FCSTD DOCUMENT  (FreeCAD 0.19R24276 (Git))
Label: Sketch_1
License: All rights reserved
LicenseURL: http://en.wikipedia.org/wiki/All_rights_reserved
objects: Sketcher::SketchObject×1, PartDesign::Body×1
note: 2 computed .brp shape members not serialized (recipe doc carries the construction recipe); baked Part::Feature solids carry a one-line shape summary decoded from their .brp

FEATURE [Sketcher::SketchObject] Sketch
  FullyConstrained = false
  MapMode = 5
  Support = -> [XY_Plane]
  sketch-geometry (21):
    g0: Circle CenterX=0 CenterY=0 CenterZ=0 NormalX=0 NormalY=0 NormalZ=1 AngleXU=0 Radius=70
    g1: Circle CenterX=0 CenterY=0 CenterZ=0 NormalX=0 NormalY=0 NormalZ=1 AngleXU=0 Radius=21.3
    g2: LineSegment StartX=-326.781 StartY=0 StartZ=0 EndX=-149.344 EndY=0 EndZ=0
    g3: Circle CenterX=-326.781 CenterY=0 CenterZ=0 NormalX=0 NormalY=0 NormalZ=1 AngleXU=0 Radius=38
    g4: Circle CenterX=-326.781 CenterY=0 CenterZ=0 NormalX=0 NormalY=0 NormalZ=1 AngleXU=0 Radius=58
    g5: LineSegment StartX=-326.781 StartY=0 StartZ=0 EndX=-280.802 EndY=35.3538 EndZ=0
    g6: Circle CenterX=-284.156 CenterY=-121.36 CenterZ=0 NormalX=0 NormalY=0 NormalZ=1 AngleXU=0 Radius=10
    g7: Circle CenterX=-254.156 CenterY=-121.36 CenterZ=0 NormalX=0 NormalY=0 NormalZ=1 AngleXU=0 Radius=10
    g8: Circle CenterX=-104.156 CenterY=-121.36 CenterZ=0 NormalX=0 NormalY=0 NormalZ=1 AngleXU=0 Radius=10
    g9: LineSegment StartX=-284.156 StartY=-121.36 StartZ=0 EndX=-104.156 EndY=-121.36 EndZ=0
    g10: GeomPoint X=-254.156 Y=-121.36 Z=0
    g11: Circle CenterX=-284.156 CenterY=-121.36 CenterZ=0 NormalX=0 NormalY=0 NormalZ=1 AngleXU=0 Radius=14
    g12: Circle CenterX=-254.156 CenterY=-121.36 CenterZ=0 NormalX=0 NormalY=0 NormalZ=1 AngleXU=0 Radius=14
    g13: Circle CenterX=-254.156 CenterY=-91.3597 CenterZ=0 NormalX=0 NormalY=0 NormalZ=1 AngleXU=0 Radius=10
    g14: Circle CenterX=-254.156 CenterY=-91.3597 CenterZ=0 NormalX=0 NormalY=0 NormalZ=1 AngleXU=0 Radius=14
    g15: LineSegment StartX=-254.156 StartY=-121.36 StartZ=0 EndX=-254.156 EndY=-91.3597 EndZ=0
    g16: LineSegment StartX=-285.794 StartY=-131.225 StartZ=0 EndX=-468.188 EndY=-131.225 EndZ=0
    g17: LineSegment StartX=-293.498 StartY=-117.793 StartZ=0 EndX=-257.551 EndY=-130.766 EndZ=0
    g18: LineSegment StartX=-254.156 StartY=-131.36 StartZ=0 EndX=-104.156 EndY=-131.36 EndZ=0
    g19: LineSegment StartX=-99.7089 StartY=-112.403 StartZ=0 EndX=-254.868 EndY=-101.334 EndZ=0
    g20: LineSegment StartX=-262.221 StartY=-85.4475 StartZ=0 EndX=-262.221 EndY=-8.34338 EndZ=0
  constraints (47):
    c: Coincident(g0,g-1)
    c: Diameter(g0) = 140
    c: Coincident(g1,g0)
    c: Diameter(g1) = 42.6
    c: PointOnObject(g2,g-1)
    c: Horizontal(g2)
    c: Coincident(g4,g3)
    c: Diameter(g3) = 76
    c: Diameter(g4) = 116
    c: Coincident(g5,g3)
    c: PointOnObject(g5,g4)
    c: Coincident(g3,g2)
    c: Equal(g6,g7)
    c: Equal(g7,g8)
    c: Diameter(g8) = 20
    c: Horizontal(g9)
    c: Coincident(g6,g9)
    c: PointOnObject(g10,g9)
    c: Coincident(g7,g10)
    c: Coincident(g8,g9)
    c: Coincident(g11,g6)
    c: Coincident(g12,g7)
    c: Diameter(g11) = 28
    c: Equal(g12,g11)
    c: DistanceX(g6,g7) = 30
    c: DistanceX(g7,g8) = 150
    c: Coincident(g14,g13)
    c: Equal(g11,g14) = 28
    c: Coincident(g15,g7)
    c: Vertical(g15)
    c: Coincident(g15,g13)
    c: DistanceY(g7,g13) = 30
    c: PointOnObject(g16,g6)
    c: Horizontal(g16)
    c: PointOnObject(g17,g6)
    c: PointOnObject(g17,g7)
    c: Tangent(g17,g7)
    c: PointOnObject(g18,g7)
    c: PointOnObject(g18,g8)
    c: Horizontal(g18)
    c: Tangent(g18,g8)
    c: PointOnObject(g19,g8)
    c: PointOnObject(g19,g13)
    c: Tangent(g19,g13)
    c: PointOnObject(g20,g13)
    c: Vertical(g20)
    c: Equal(g13,g7)
FEATURE [PartDesign::Body] Body
  Group = -> [Sketch]
  Origin = -> Origin
